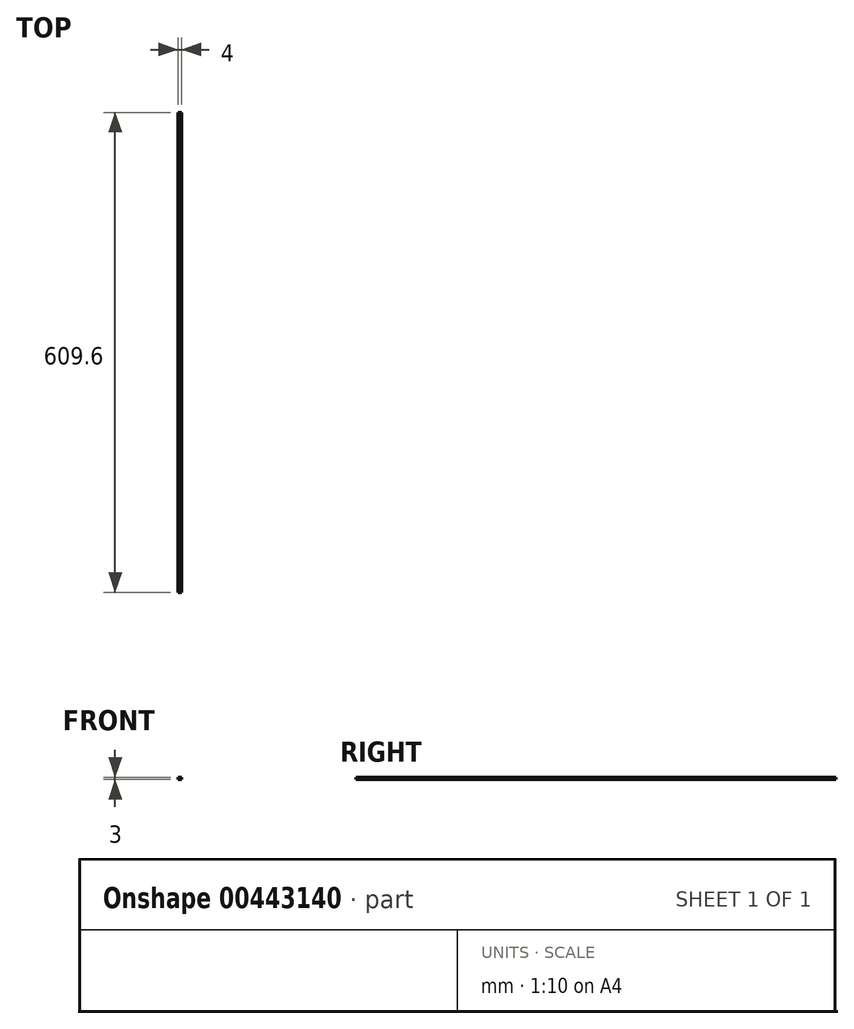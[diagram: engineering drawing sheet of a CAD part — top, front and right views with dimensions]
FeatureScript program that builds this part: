
annotation { "Feature Type Name" : "Feature", "Feature Type Description" : "" }
export const myFeature = defineFeature(function(context is Context, id is Id, definition is map)
    precondition{}
    {
        {
            var Q0;
            Q0=qCreatedBy(makeId("Top.planeOp"),FACE);
            var sketch = newSketch(context, id + "F0", { "sketchPlane" : qUnion([Q0])});
            skLineSegment(sketch, "E0.bottom", {"start": v(-4, -343.9) * mm, "end": v(0, -343.9) * mm});
            skLineSegment(sketch, "E0.top", {"start": v(-4, 265.7) * mm, "end": v(0, 265.7) * mm});
            skLineSegment(sketch, "E0.left", {"start": v(-4, -343.9) * mm, "end": v(-4, 265.7) * mm});
            skLineSegment(sketch, "E0.right", {"start": v(0, -343.9) * mm, "end": v(0, 265.7) * mm});
            skSolve(sketch);
        }
        {
            var Q0;
            Q0=makeQuery(id+"F0.imprint","IMPRINT",FACE,{"disambiguationData":[TD([[makeQuery(id+"F0.imprint","IMPRINT",EDGE,{"derivedFrom":sQuery(id+"F0.wireOp",EDGE,"E0.bottom")}),1.0]])]});
            extrude(context, id + "F1", {"entities" : qUnion([Q0]), "depth" : 3 * mm});
        }
    });
